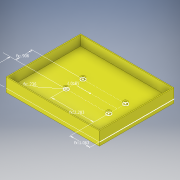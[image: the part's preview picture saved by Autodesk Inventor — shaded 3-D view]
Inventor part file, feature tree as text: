
AUTODESK INVENTOR PART (.ipt)
format: ipt  version: 2019.4 (Build 234330000, 330)  size: 180,736 bytes
history: native  units: in
note: dims shown in document units (in); Inventor stores cm internally (conversion verified against a paired STEP export)
features: sketch x5, extrude x3, hole x1
ambient origin geometry x8: Origin, YZ Plane, XZ Plane, XY Plane, X Axis, Y Axis, Z Axis, Center Point
bodies: Solid1 (feature_tree)
feature tree (9):
  extrude  "Extrusion1"  Depth=4.0in
  extrude  "Extrusion12"  Depth=0.2in
  hole  "Hole17"  [1 undecoded]
  extrude  "Extrusion13"  Depth=0.1in
  sketch  "Sketch1"  dims[d0=5.0in d1=4.0in]
  sketch  "Sketch22"  dims[d2=0.2in d3=0.0in d173=2.2835in]
  sketch  "Sketch26"  dims[d174=0.9055in d175=1.563in]
  sketch  "Sketch27"  dims[d176=0.2362in d177=0.1in]
  sketch  "Sketch28"  dims[d178=0.0in d179=0.096in d180=0.75in d181=0.1285in d182=0.157in d183=0.5635in d184=1.0in d185=0.8108in d186=0.05in d187=0.05in d188=0.515in d189=0.0in d190=1.063in]
note: 1 required parameter value undecoded (feature->parameter linkage not recoverable at this tier; creation-order binding heuristic only, values carry confidence <= 0.55)
